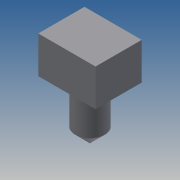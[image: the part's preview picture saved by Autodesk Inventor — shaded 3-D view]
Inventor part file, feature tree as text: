
AUTODESK INVENTOR PART (.ipt)
format: ipt  version: 2013 (Build 170138000, 138)  size: 82,944 bytes
history: native  units: mm
features: sketch x2, revolve x1, extrude x1
ambient origin geometry x8: Origin, YZ Plane, XZ Plane, XY Plane, X Axis, Y Axis, Z Axis, Center Point
bodies: Solid1 (feature_tree)
feature tree (4):
  revolve  "Revolution1"  [1 undecoded]
  extrude  "Extrusion1"  TaperAngle=90.0deg  [1 undecoded]
  sketch  "Sketch1"  dims[d0=50.0mm d1=8.0mm]
  sketch  "Sketch2"  dims[d2=135.0deg d3=90.0deg d4=31.0mm d6=25.0mm d7=20.0mm d8=0.0mm]
note: 2 required parameter values undecoded (feature->parameter linkage not recoverable at this tier; creation-order binding heuristic only, values carry confidence <= 0.55)